# Revit family: 34-HC_RAV_HCL_TOSHIBA_RM1CTP_110-140
name_source: partatom
category: Mechanical Equipment
revit_build: Autodesk Revit 2017 (Build: 20160225_1515(x64)
units: mm (PartAtom-declared; Revit-internal decimal feet)

## family parameters
Always vertical = Yes
Cut with Voids When Loaded = No
OmniClass Number = 23.75.00.00
OmniClass Title = Climate Control (HVAC)
Part Type = Normal
Room Calculation Point = No
Round Connector Dimension = Use Diameter
Shared = No
Work Plane-Based = No

## types (3) — shared parameters
Air filter = Long life filter
Casing material = -
Content Supplier URL = www.hcltech.com
Depth (mm) = 690 mm  [stored 2.26378 ft]
Drain Pipe Diameter (mm) = 26 mm
Duct Diameter (mm) = -
EMCS = 4
ETIM Article Class = EC001213
Height (mm) = 235 mm
Hydronic Return Diameter (mm) = 16 mm  [stored 0.0524934 ft]
Hydronic Supply Diameter (mm) = 10 mm  [stored 0.0328084 ft]
MCA (A) = -
MEPcontent Class = HEATPUMP
MOCP (A) = 25
Manufacturer = Toshiba
Manufacturer URL = https://www.toshiba-carrier.co.jp
Operating range - Cooling (°C) = 21 - 32
Operating range - Heating (°C) = 0 - 28
Part load = -
Piping cnnection = Flare
Product Line = TCTC
Red = Colour RGB-250 000 000
Revit Version = 2017
Static pressure (Pa) = -
URL = https://www.toshiba-carrier.co.jp
Weight (Kg) = 37
White = Colour- RGB 255 255  255
Width (mm) = 1586 mm  [stored 5.20341 ft]

## per-type parameters (varying)
| type | Airflow (m3/h) | Article Description | Description | Energy Class- Cooling/Heating | Frequency (Hz) | Pdesign-Cooling/Heating | Power consumption-Cooling (Kw) | Power consumption-Heating (Kw) | Rated Capacity -Cooling/Heating  (kW) | Rated Power Consumption | Rated efficiency - EER / COP | Refrigerant Information | Running current-Cooling (A) | Running current-Heating (A) | Seasonal & Rated efficiency-SEER  / SCOP | Sound pressure - High (dB) | Sound pressure - Low (dB) | Sound pressure - Mid (dB) | Starting current (A) | Voltage (V) |
| RAV-RM1101CTP-E | 1860 | R32 Ceiling | R32 Ceiling | A+ / A+ | 50Hz | 9.5 / 7.6 | 2.23 | 2.38 | 9.5 / 11.2 | 2.95 / 2.94 | 3.22 / 3.81 | R32 / R410A | 10.67 - 9.78 | 11.39 - 10.44 | 5.86 / 4.27 | 44 | 32 | 38 | 21 | 220-240V |
| RAV-RM1401CTP-E | 2040 | R32 Ceiling | R32 Ceiling | - | 50 | - | 3.58 | 3.59 | 12.5 / 14.0 | 3.58 / 3.59 | 3.49 / 3.90 | R32 / R410A | 17.13 - 15.70 | 17.18 - 15.75 | - | 46 | 35 | 41 | 21.6 | 220-240 |
| RAV-RM1601CTP-E | 2040 | R410A Ceiling | R410A Ceiling | - | 3Phase  , 50 | - | 4.50 | 4.31 | 14.0 / 16.0 | 4.50 / 4.31 | 3.11 / 3.71 | R410A | 7.60 - 6.96 | 7.28 - 6.66 | - | 46 | 36 | 42 | 16.1 | 380-415 |

note: column(s) folded — value = type name in every type: Article Type, Manufacturer Art. No., Model

note: [stored X ft] marks values corroborated as IEEE doubles in the binary element streams (Revit-internal decimal feet)

## geometry (parser evidence)
native form markers: Sweep x6
no freeform markers — native parametric forms only
